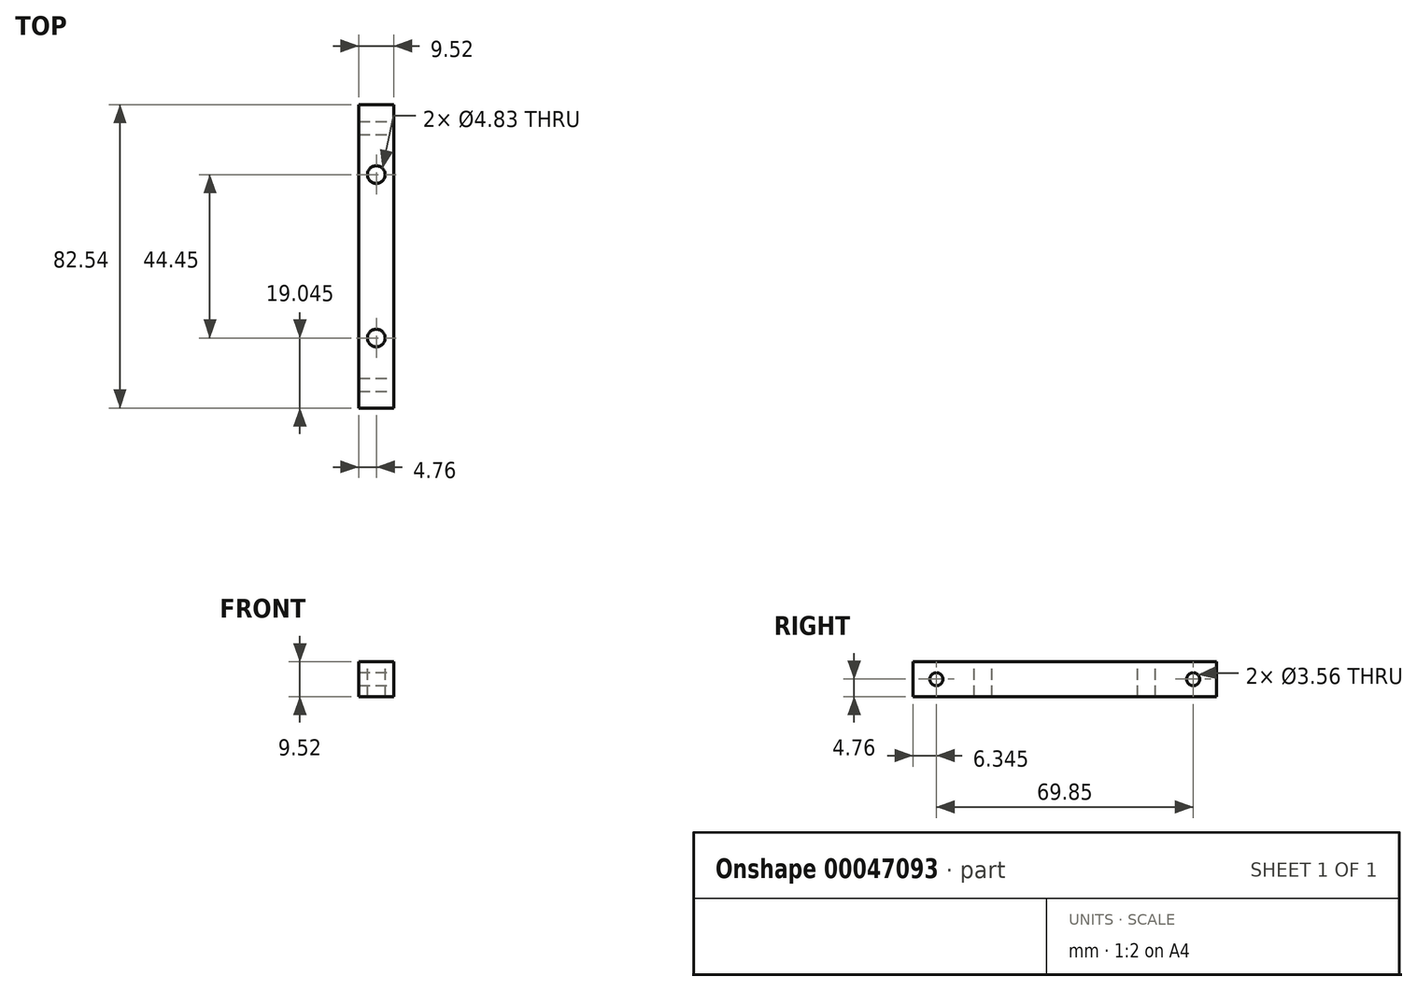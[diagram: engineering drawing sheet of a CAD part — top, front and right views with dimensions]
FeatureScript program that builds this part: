
annotation { "Feature Type Name" : "Feature", "Feature Type Description" : "" }
export const myFeature = defineFeature(function(context is Context, id is Id, definition is map)
    precondition{}
    {
        {
            var Q0;
            Q0=qCreatedBy(makeId("Front.planeOp"),FACE);
            var sketch = newSketch(context, id + "F0", { "sketchPlane" : qUnion([Q0])});
            skLineSegment(sketch, "E0.rect.bottom", {"start": v(4.76, 4.76) * mm, "end": v(-4.76, 4.76) * mm});
            skLineSegment(sketch, "E0.rect.top", {"start": v(4.76, -4.76) * mm, "end": v(-4.76, -4.76) * mm});
            skLineSegment(sketch, "E0.rect.left", {"start": v(4.76, 4.76) * mm, "end": v(4.76, -4.76) * mm});
            skLineSegment(sketch, "E0.rect.right", {"start": v(-4.76, 4.76) * mm, "end": v(-4.76, -4.76) * mm});
            skPoint(sketch, "E0.rect.middle", {"position": v(0, 0) * mm});
            skSolve(sketch);
        }
        {
            var Q0;
            Q0 = qSketchRegion(id + "F0", true);
            extrude(context, id + "F1", {"entities" : qUnion([Q0]), "endBound" : BoundingType.SYMMETRIC, "depth" : 82.55 * mm});
        }
        {
            var Q0;
            Q0=qCreatedBy(makeId("Right.planeOp"),FACE);
            var sketch = newSketch(context, id + "F2", { "sketchPlane" : qUnion([Q0])});
            skCircle(sketch, "E1", {"center": v(34.93, 0) * mm, "radius": 1.78 * mm});
            skCircle(sketch, "E2", {"center": v(-34.93, 0) * mm, "radius": 1.78 * mm});
            skSolve(sketch);
        }
        {
            var Q0;
            Q0 = qSketchRegion(id + "F2", true);
            extrude(context, id + "F3", {"entities" : qUnion([Q0]), "operationType" : NewBodyOperationType.REMOVE, "endBound" : BoundingType.SYMMETRIC, "oppositeDirection" : true, "depth" : 22.22 * mm});
        }
        {
            var Q0;
            Q0=qCreatedBy(makeId("Top.planeOp"),FACE);
            var sketch = newSketch(context, id + "F4", { "sketchPlane" : qUnion([Q0])});
            skCircle(sketch, "E3", {"center": v(0, 22.23) * mm, "radius": 2.41 * mm});
            skCircle(sketch, "E4", {"center": v(0, -22.23) * mm, "radius": 2.41 * mm});
            skSolve(sketch);
        }
        {
            var Q0;
            Q0 = qSketchRegion(id + "F4", true);
            extrude(context, id + "F5", {"entities" : qUnion([Q0]), "operationType" : NewBodyOperationType.REMOVE, "endBound" : BoundingType.SYMMETRIC, "oppositeDirection" : true, "depth" : 22.22 * mm});
        }
    });
